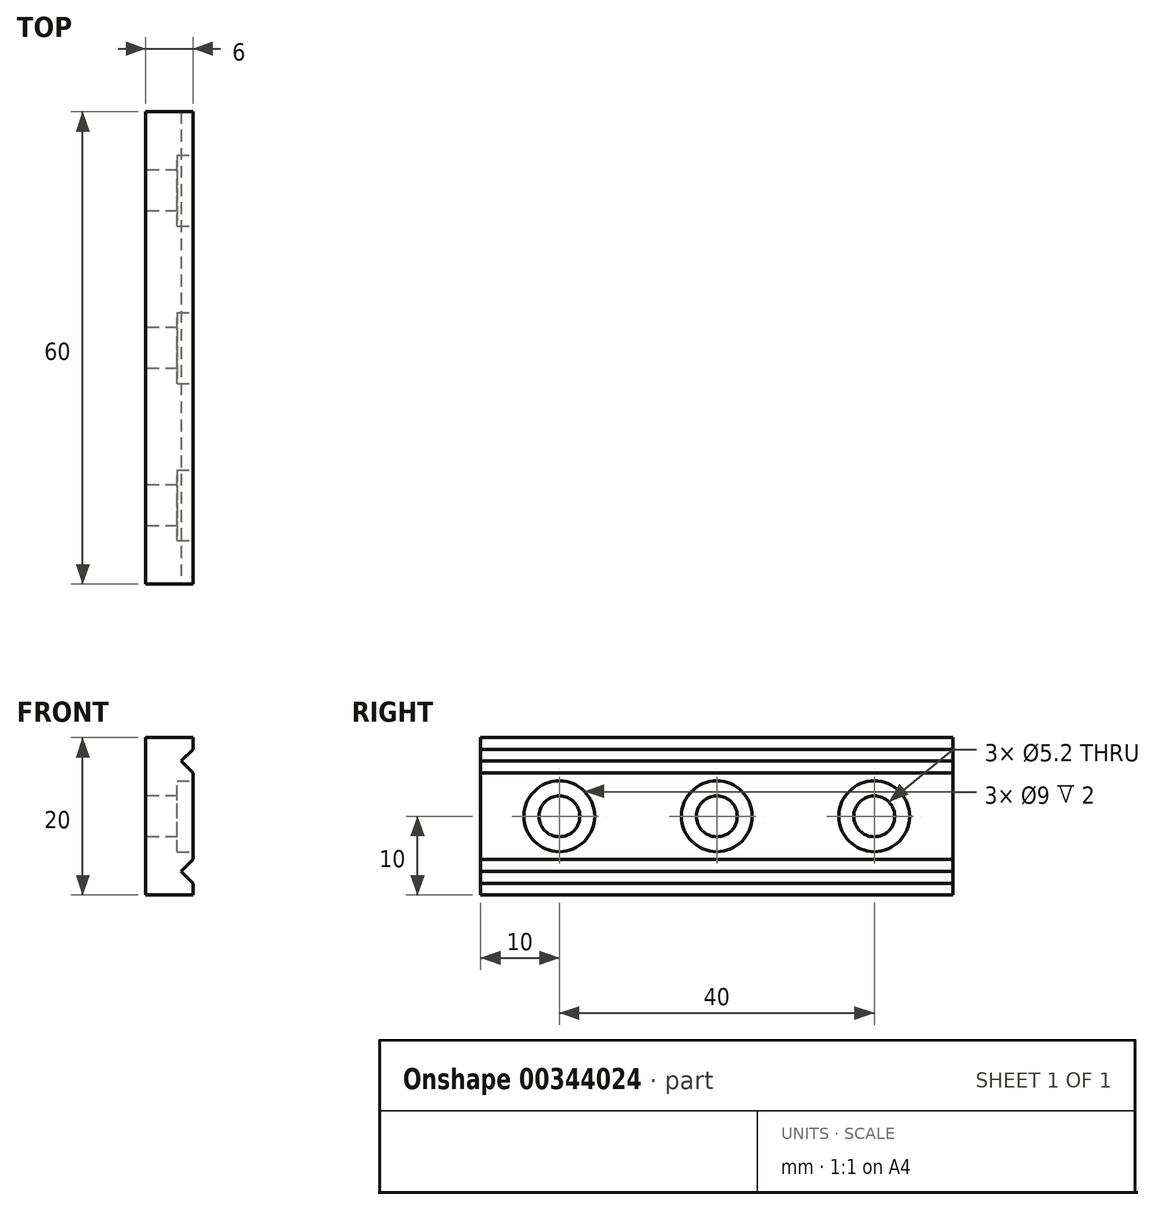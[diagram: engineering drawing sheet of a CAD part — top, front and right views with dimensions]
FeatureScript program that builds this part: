
annotation { "Feature Type Name" : "Feature", "Feature Type Description" : "" }
export const myFeature = defineFeature(function(context is Context, id is Id, definition is map)
    precondition{}
    {
        {
            var Q0;
            Q0=qCreatedBy(makeId("Right.planeOp"),FACE);
            var sketch = newSketch(context, id + "F0", { "sketchPlane" : qUnion([Q0])});
            skLineSegment(sketch, "E0.bottom", {"start": v(30, -10) * mm, "end": v(-30, -10) * mm});
            skLineSegment(sketch, "E0.top", {"start": v(30, 10) * mm, "end": v(-30, 10) * mm});
            skLineSegment(sketch, "E0.left", {"start": v(30, -10) * mm, "end": v(30, 10) * mm});
            skLineSegment(sketch, "E0.right", {"start": v(-30, -10) * mm, "end": v(-30, 10) * mm});
            skPoint(sketch, "E0.middle", {"position": v(0, 0) * mm});
            skCircle(sketch, "E1", {"center": v(-20, 0) * mm, "radius": 2.6 * mm});
            skCircle(sketch, "E2", {"center": v(20, 0) * mm, "radius": 2.6 * mm});
            skCircle(sketch, "E3", {"center": v(0, 0) * mm, "radius": 2.6 * mm});
            skSolve(sketch);
        }
        {
            var Q0;
            Q0=makeQuery(id+"F0.imprint","IMPRINT",FACE,{"disambiguationData":[TD([[makeQuery(id+"F0.imprint","IMPRINT",EDGE,{"derivedFrom":sQuery(id+"F0.wireOp",EDGE,"E0.bottom")}),-1.0]])]});
            extrude(context, id + "F1", {"entities" : qUnion([Q0]), "depth" : 6 * mm});
        }
        {
            var Q0;
            Q0=makeQuery(id+"F1.opExtrude","CAP_FACE",FACE,{"disambiguationData":[OSD([sQuery(id+"F0.wireOp",EDGE,"E0.bottom"),sQuery(id+"F0.wireOp",EDGE,"E0.top"),sQuery(id+"F0.wireOp",EDGE,"E0.left"),sQuery(id+"F0.wireOp",EDGE,"E0.right"),sQuery(id+"F0.wireOp",EDGE,"E1"),sQuery(id+"F0.wireOp",EDGE,"E2"),sQuery(id+"F0.wireOp",EDGE,"E3")])],"isStart":false});
            var sketch = newSketch(context, id + "F2", { "sketchPlane" : qUnion([Q0])});
            skCircle(sketch, "E4", {"center": v(-20, 0) * mm, "radius": 4.5 * mm});
            skCircle(sketch, "E5", {"center": v(0, 0) * mm, "radius": 4.5 * mm});
            skCircle(sketch, "E6", {"center": v(20, 0) * mm, "radius": 4.5 * mm});
            skSolve(sketch);
        }
        {
            var Q0;
            Q0 = qSketchRegion(id + "F2", true);
            extrude(context, id + "F3", {"entities" : qUnion([Q0]), "operationType" : NewBodyOperationType.REMOVE, "oppositeDirection" : true, "depth" : 2 * mm});
        }
        {
            var Q0;
            Q0=makeQuery(id+"F1.opExtrude","SWEPT_FACE",FACE,{"disambiguationData":[OSD([sQuery(id+"F0.wireOp",EDGE,"E0.right")])]});
            var sketch = newSketch(context, id + "F4", { "sketchPlane" : qUnion([Q0])});
            skLineSegment(sketch, "E7", {"start": v(4.5, 7) * mm, "end": v(6.79, 9.29) * mm});
            skLineSegment(sketch, "E8", {"start": v(4.5, 7) * mm, "end": v(7.4, 4.1) * mm});
            skLineSegment(sketch, "E9", {"start": v(4.5, -7) * mm, "end": v(7.13, -4.37) * mm});
            skLineSegment(sketch, "E10", {"start": v(4.5, -7) * mm, "end": v(10.17, -12.67) * mm});
            skSolve(sketch);
        }
        {
            var Q0;
            {var subQ0=sQuery(id+"F4.wireOp",EDGE,"E8");var subQ1=sQuery(id+"F4.wireOp",EDGE,"E7");var subQ2=makeQuery(id+"F4.imprint","INTERSECT",VERTEX,{"derivedFrom":[subQ1,subQ0]});Q0=makeQuery(id+"F4.imprint","IMPRINT",FACE,{"disambiguationData":[TD([[makeQuery(id+"F4.imprint","IMPRINT",EDGE,{"disambiguationData":[TD([[subQ2,-1.0]])],"derivedFrom":subQ1}),-1.0]])]});}
            var Q1;
            {var subQ0=sQuery(id+"F4.wireOp",EDGE,"E10");var subQ1=sQuery(id+"F4.wireOp",EDGE,"E9");var subQ2=makeQuery(id+"F4.imprint","INTERSECT",VERTEX,{"derivedFrom":[subQ1,subQ0]});Q1=makeQuery(id+"F4.imprint","IMPRINT",FACE,{"disambiguationData":[TD([[makeQuery(id+"F4.imprint","IMPRINT",EDGE,{"disambiguationData":[TD([[subQ2,-1.0]])],"derivedFrom":subQ1}),-1.0]])]});}
            extrude(context, id + "F5", {"entities" : qUnion([Q0, Q1]), "operationType" : NewBodyOperationType.REMOVE, "endBound" : BoundingType.THROUGH_ALL, "oppositeDirection" : true, "depth" : 25 * mm});
        }
    });
